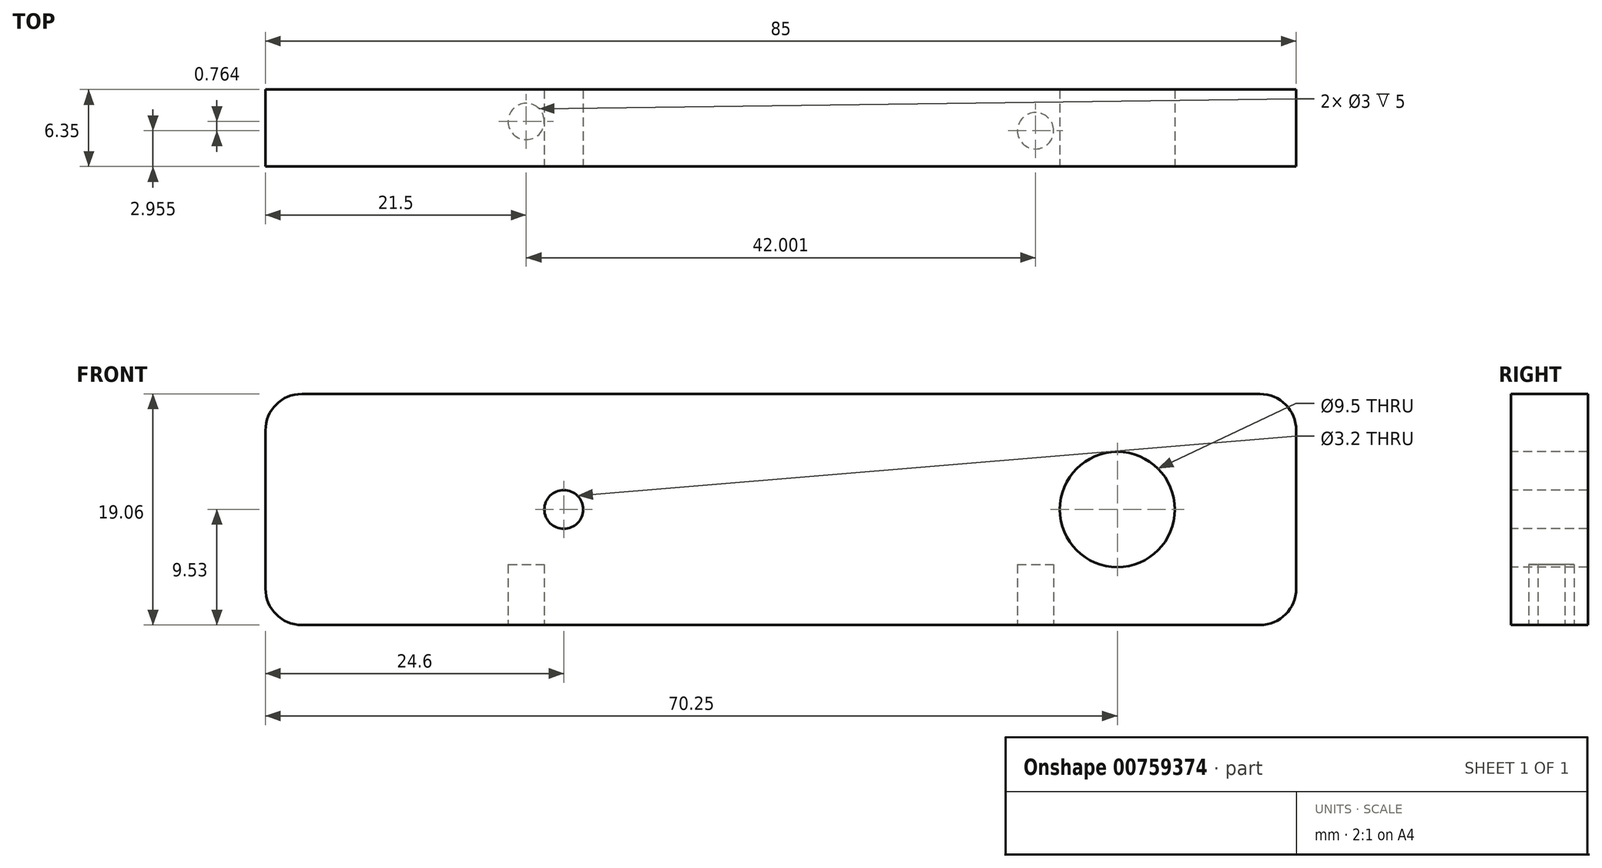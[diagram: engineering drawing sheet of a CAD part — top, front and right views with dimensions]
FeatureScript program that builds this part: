
annotation { "Feature Type Name" : "Feature", "Feature Type Description" : "" }
export const myFeature = defineFeature(function(context is Context, id is Id, definition is map)
    precondition{}
    {
        {
            var Q0;
            Q0=qCreatedBy(makeId("Front.planeOp"),FACE);
            var sketch = newSketch(context, id + "F0", { "sketchPlane" : qUnion([Q0])});
            skLineSegment(sketch, "E0.bottom", {"start": v(42.5, -9.52) * mm, "end": v(-42.5, -9.53) * mm});
            skLineSegment(sketch, "E0.top", {"start": v(42.5, 9.53) * mm, "end": v(-42.5, 9.52) * mm});
            skLineSegment(sketch, "E0.left", {"start": v(42.5, -9.52) * mm, "end": v(42.5, 9.53) * mm});
            skLineSegment(sketch, "E0.right", {"start": v(-42.5, -9.53) * mm, "end": v(-42.5, 9.53) * mm});
            skPoint(sketch, "E0.middle", {"position": v(0, 0) * mm});
            skSolve(sketch);
        }
        {
            var Q0;
            Q0=makeQuery(id+"F0.imprint","IMPRINT",FACE,{"disambiguationData":[TD([[makeQuery(id+"F0.imprint","IMPRINT",EDGE,{"derivedFrom":sQuery(id+"F0.wireOp",EDGE,"E0.bottom")}),-1.0]])]});
            extrude(context, id + "F1", {"entities" : qUnion([Q0]), "depth" : 6.35 * mm, "offsetDistance" : 25 * mm});
        }
        {
            var Q0;
            Q0=makeQuery(id+"F1.opExtrude","SWEPT_EDGE",EDGE,{"disambiguationData":[OSD([sQuery(id+"F0.wireOp",EDGE,"E0.top"),sQuery(id+"F0.wireOp",EDGE,"E0.right")])]});
            var Q1;
            Q1=makeQuery(id+"F1.opExtrude","SWEPT_EDGE",EDGE,{"disambiguationData":[OSD([sQuery(id+"F0.wireOp",EDGE,"E0.top"),sQuery(id+"F0.wireOp",EDGE,"E0.left")])]});
            var Q2;
            Q2=makeQuery(id+"F1.opExtrude","SWEPT_EDGE",EDGE,{"disambiguationData":[OSD([sQuery(id+"F0.wireOp",EDGE,"E0.bottom"),sQuery(id+"F0.wireOp",EDGE,"E0.left")])]});
            var Q3;
            Q3=makeQuery(id+"F1.opExtrude","SWEPT_EDGE",EDGE,{"disambiguationData":[OSD([sQuery(id+"F0.wireOp",EDGE,"E0.bottom"),sQuery(id+"F0.wireOp",EDGE,"E0.right")])]});
            fillet(context, id + "F2", {"entities" : qUnion([Q0, Q1, Q2, Q3]), "radius" : 3 * mm, "tangentPropagation" : true, "allowEdgeOverflow" : false});
        }
        {
            var Q0;
            Q0=makeQuery(id+"F1.opExtrude","CAP_FACE",FACE,{"disambiguationData":[OSD([sQuery(id+"F0.wireOp",EDGE,"E0.bottom"),sQuery(id+"F0.wireOp",EDGE,"E0.top"),sQuery(id+"F0.wireOp",EDGE,"E0.left"),sQuery(id+"F0.wireOp",EDGE,"E0.right")])],"isStart":false});
            var sketch = newSketch(context, id + "F3", { "sketchPlane" : qUnion([Q0])});
            skCircle(sketch, "E1", {"center": v(-17.9, 0) * mm, "radius": 1.6 * mm});
            skCircle(sketch, "E2", {"center": v(27.75, 0) * mm, "radius": 4.75 * mm});
            skSolve(sketch);
        }
        {
            var Q0;
            Q0=makeQuery(id+"F1.opExtrude","SWEPT_FACE",FACE,{"disambiguationData":[OSD([sQuery(id+"F0.wireOp",EDGE,"E0.bottom")])]});
            var sketch = newSketch(context, id + "F4", { "sketchPlane" : qUnion([Q0])});
            skCircle(sketch, "E3", {"center": v(-21, 2.63) * mm, "radius": 1.5 * mm});
            skCircle(sketch, "E4", {"center": v(21, 3.4) * mm, "radius": 1.5 * mm});
            skSolve(sketch);
        }
        {
            var Q0;
            Q0=makeQuery(id+"F4.imprint","IMPRINT",FACE,{"disambiguationData":[TD([[makeQuery(id+"F4.imprint","IMPRINT",EDGE,{"derivedFrom":sQuery(id+"F4.wireOp",EDGE,"E3")}),1.0]])]});
            var Q1;
            Q1=makeQuery(id+"F4.imprint","IMPRINT",FACE,{"disambiguationData":[TD([[makeQuery(id+"F4.imprint","IMPRINT",EDGE,{"derivedFrom":sQuery(id+"F4.wireOp",EDGE,"E4")}),1.0]])]});
            extrude(context, id + "F5", {"entities" : qUnion([Q0, Q1]), "operationType" : NewBodyOperationType.REMOVE, "oppositeDirection" : true, "depth" : 5 * mm, "offsetDistance" : 25 * mm});
        }
        {
            var Q0;
            Q0=makeQuery(id+"F3.imprint","IMPRINT",FACE,{"disambiguationData":[TD([[makeQuery(id+"F3.imprint","IMPRINT",EDGE,{"derivedFrom":sQuery(id+"F3.wireOp",EDGE,"E1")}),1.0]])]});
            var Q1;
            Q1=makeQuery(id+"F3.imprint","IMPRINT",FACE,{"disambiguationData":[TD([[makeQuery(id+"F3.imprint","IMPRINT",EDGE,{"derivedFrom":sQuery(id+"F3.wireOp",EDGE,"E2")}),1.0]])]});
            var Q2;
            Q2=sQuery(id+"F3.wireOp",EDGE,"E2");
            var Q3;
            Q3=sQuery(id+"F3.wireOp",EDGE,"E1");
            extrude(context, id + "F6", {"entities" : qUnion([Q0, Q1]), "operationType" : NewBodyOperationType.REMOVE, "surfaceEntities" : qUnion([Q2, Q3]), "oppositeDirection" : true, "depth" : 25 * mm, "offsetDistance" : 25 * mm});
        }
    });
